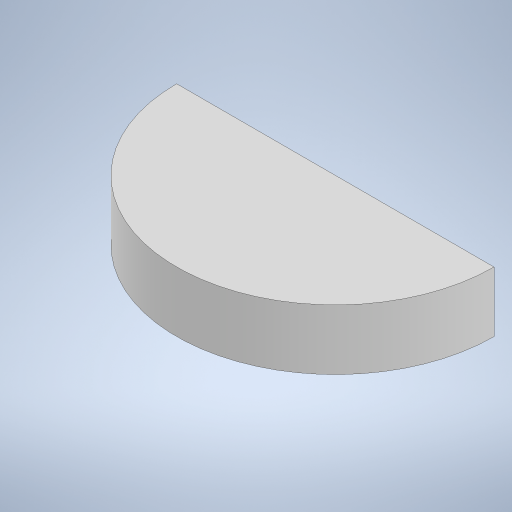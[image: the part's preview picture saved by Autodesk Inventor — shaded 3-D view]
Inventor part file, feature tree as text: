
AUTODESK INVENTOR PART (.ipt)
format: ipt  version: 2024 (Build 280153000, 153)  size: 219,136 bytes
history: native  units: mm
features: other x1, revolve x1, sketch x1
ambient origin geometry x8: Origin, YZ Plane, XZ Plane, XY Plane, X Axis, Y Axis, Z Axis, Center Point
bodies: Body1 (feature_tree)
feature tree (3):
  other  "Sólido1"
  revolve  "Revolución1"  [1 undecoded]
  sketch  "Boceto1"  dims[d0=38.0mm d1=100.0mm d2=3.2mm d3=35.0mm d4=3.4mm d5=3.2mm d6=180.0deg d7=0.872665mm]
note: 1 required parameter value undecoded (feature->parameter linkage not recoverable at this tier; creation-order binding heuristic only, values carry confidence <= 0.55)
